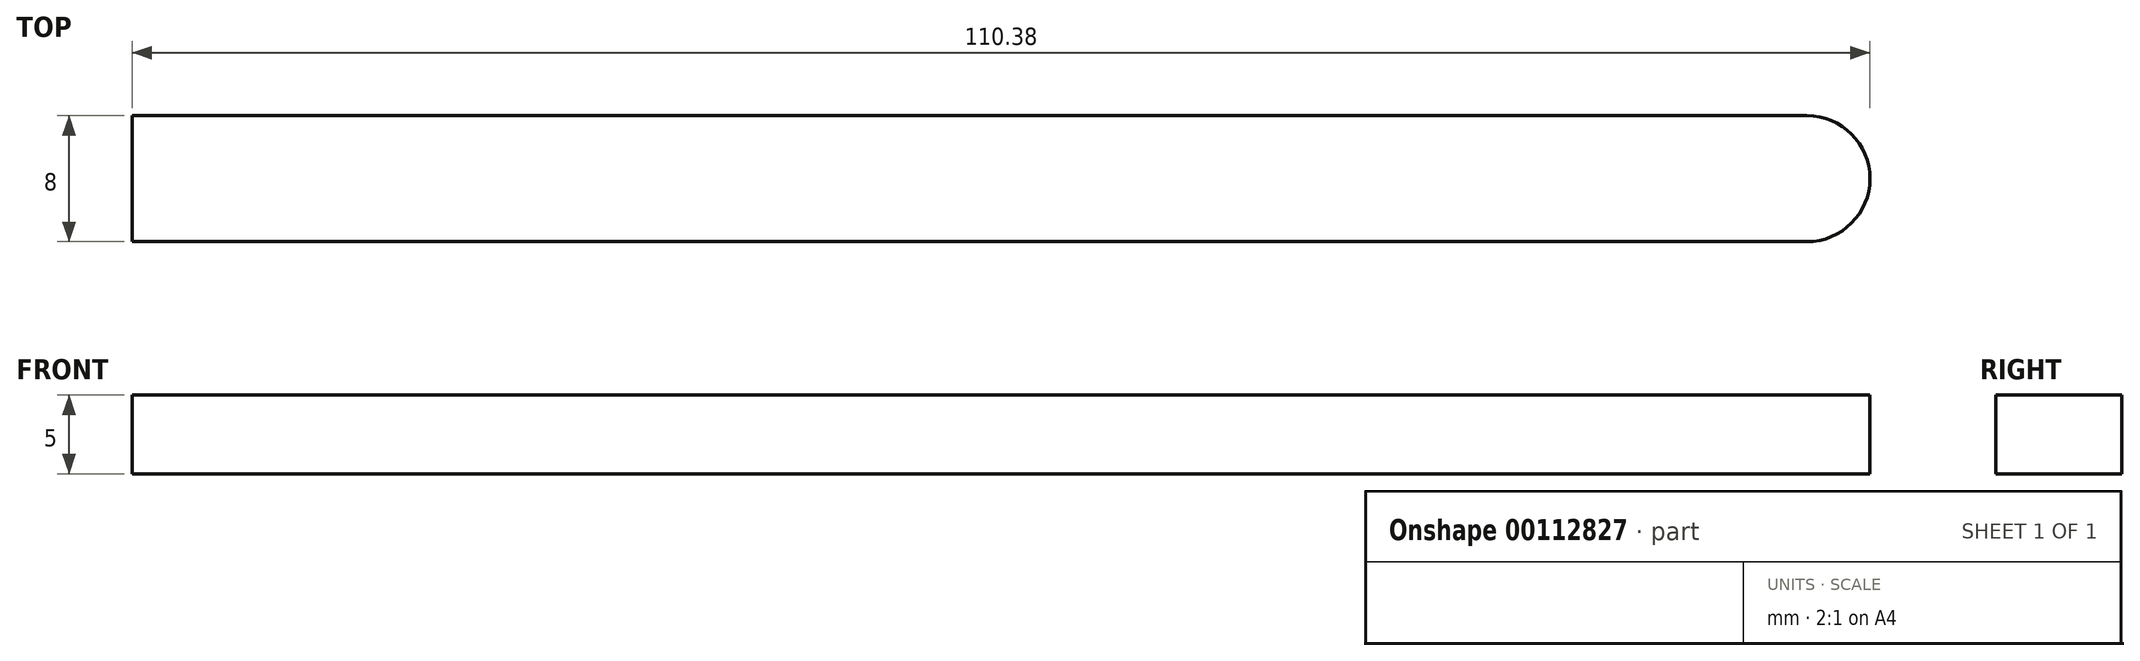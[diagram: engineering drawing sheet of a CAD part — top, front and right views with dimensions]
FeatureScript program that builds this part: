
annotation { "Feature Type Name" : "Feature", "Feature Type Description" : "" }
export const myFeature = defineFeature(function(context is Context, id is Id, definition is map)
    precondition{}
    {
        {
            var Q0;
            Q0=qCreatedBy(makeId("Top.planeOp"),FACE);
            var sketch = newSketch(context, id + "F0", { "sketchPlane" : qUnion([Q0])});
            skLineSegment(sketch, "E0.bottom", {"start": v(-60.94, 0) * mm, "end": v(45.44, 0) * mm});
            skLineSegment(sketch, "E0.top", {"start": v(-60.94, 8) * mm, "end": v(45.44, 8) * mm});
            skLineSegment(sketch, "E0.left", {"start": v(-60.94, 0) * mm, "end": v(-60.94, 8) * mm});
            skLineSegment(sketch, "E0.right", {"start": v(49.44, 4) * mm, "end": v(49.44, 4) * mm});
            skPoint(sketch, "E1.visualSharp", {"position": v(49.44, 8) * mm});
            skArc(sketch, "E1.filletArc", {"start": v(49.44, 4) * mm, "mid": v(48.27, 6.83) * mm, "end": v(45.44, 8) * mm});
            skPoint(sketch, "E2.visualSharp", {"position": v(49.44, 0) * mm});
            skArc(sketch, "E2.filletArc", {"start": v(45.44, 0) * mm, "mid": v(48.27, 1.17) * mm, "end": v(49.44, 4) * mm});
            skSolve(sketch);
        }
        {
            var Q0;
            Q0 = qSketchRegion(id + "F0", true);
            extrude(context, id + "F1", {"entities" : qUnion([Q0]), "depth" : 5 * mm});
        }
    });
